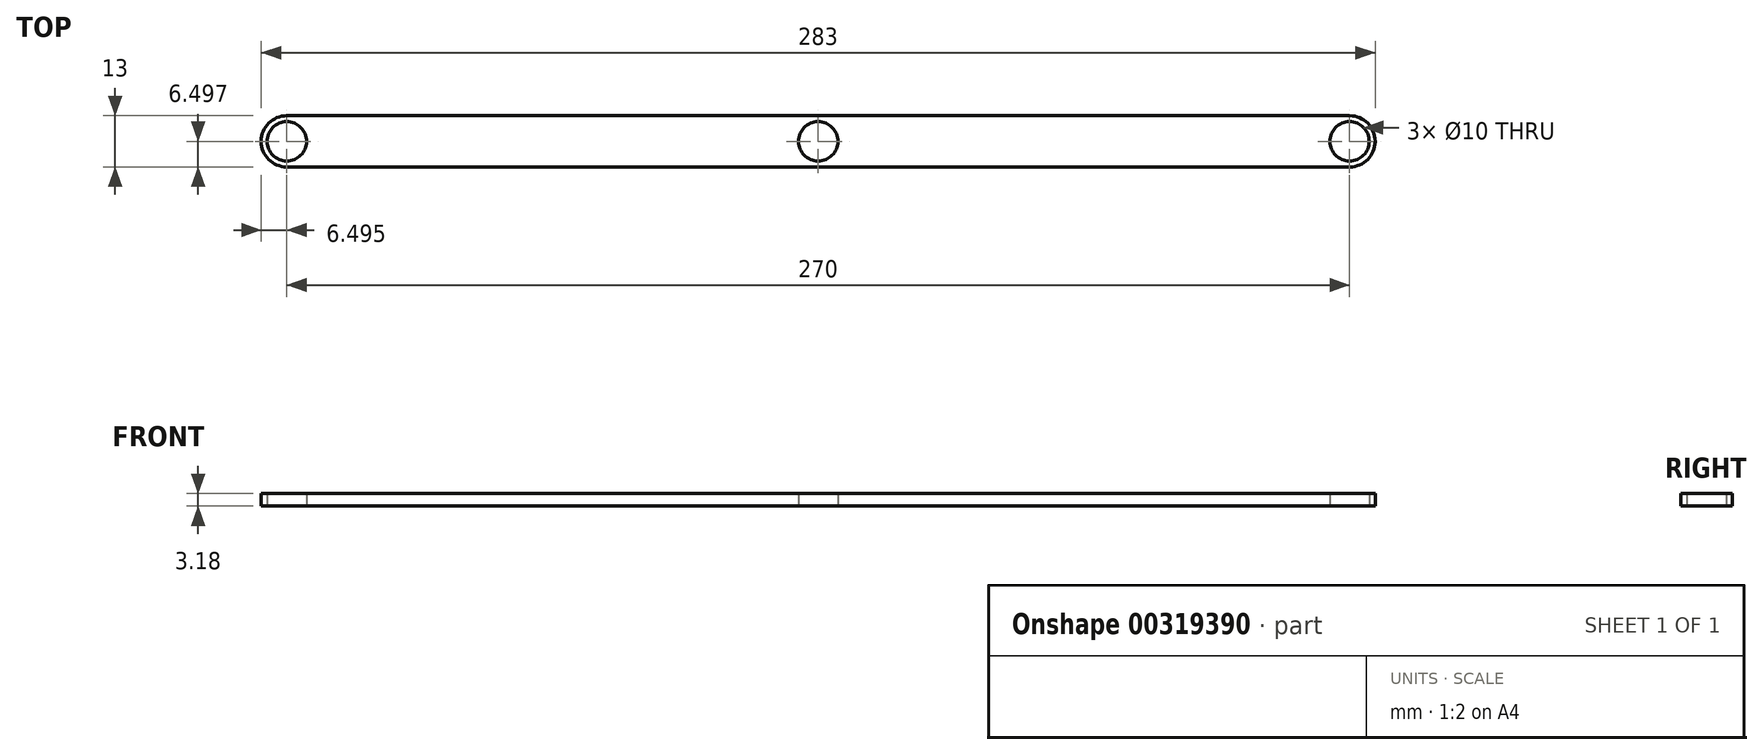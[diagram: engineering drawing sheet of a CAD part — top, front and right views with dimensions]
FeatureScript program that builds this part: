
annotation { "Feature Type Name" : "Feature", "Feature Type Description" : "" }
export const myFeature = defineFeature(function(context is Context, id is Id, definition is map)
    precondition{}
    {
        {
            var Q0;
            Q0=qCreatedBy(makeId("Top.planeOp"),FACE);
            var sketch = newSketch(context, id + "F0", { "sketchPlane" : qUnion([Q0])});
            skArc(sketch, "E0", {"start": v(-148.33, 25.07) * mm, "mid": v(-154.83, 18.57) * mm, "end": v(-148.33, 12.07) * mm});
            skCircle(sketch, "E1", {"center": v(-148.33, 18.57) * mm, "radius": 5 * mm});
            skLineSegment(sketch, "E2", {"start": v(-148.33, 25.07) * mm, "end": v(-80.83, 25.07) * mm});
            skLineSegment(sketch, "E3.MirrorCS", {"start": v(-148.33, 12.07) * mm, "end": v(-80.83, 12.07) * mm});
            skPoint(sketch, "E4.end.orphan", {"position": v(-80.83, 12.07) * mm});
            skPoint(sketch, "E4.start.orphan", {"position": v(-80.83, 25.07) * mm});
            skLineSegment(sketch, "E5.MirrorCS", {"start": v(-13.33, 12.07) * mm, "end": v(-80.83, 12.07) * mm});
            skLineSegment(sketch, "E6.MirrorCS", {"start": v(-13.33, 25.07) * mm, "end": v(-80.83, 25.07) * mm});
            skCircle(sketch, "E7.MirrorC", {"center": v(-13.33, 18.57) * mm, "radius": 5 * mm});
            skLineSegment(sketch, "E8.MirrorCS", {"start": v(-13.33, 25.07) * mm, "end": v(54.17, 25.07) * mm});
            skLineSegment(sketch, "E9.MirrorCS", {"start": v(-13.33, 12.07) * mm, "end": v(54.17, 12.07) * mm});
            skLineSegment(sketch, "E10.MirrorCS", {"start": v(121.67, 12.07) * mm, "end": v(54.17, 12.07) * mm});
            skLineSegment(sketch, "E11.MirrorCS", {"start": v(121.67, 25.07) * mm, "end": v(54.17, 25.07) * mm});
            skArc(sketch, "E12.MirrorCS", {"start": v(121.67, 25.07) * mm, "mid": v(128.17, 18.57) * mm, "end": v(121.67, 12.07) * mm});
            skCircle(sketch, "E13.MirrorC", {"center": v(121.67, 18.57) * mm, "radius": 5 * mm});
            skPoint(sketch, "E14.orphan", {"position": v(-13.33, 25.07) * mm});
            skPoint(sketch, "E15.MirrorCS.end.orphan", {"position": v(-13.33, 12.07) * mm});
            skSolve(sketch);
        }
        {
            var Q0;
            {var subQ1=sQuery(id+"F0.wireOp",EDGE,"E2");Q0=makeQuery(id+"F0.imprint","IMPRINT",FACE,{"disambiguationData":[TD([[makeQuery(id+"F0.imprint","IMPRINT",EDGE,{"derivedFrom":subQ1}),-1.0]])]});}
            var Q1;
            {var subQ0=sQuery(id+"F0.wireOp",EDGE,"E0");Q1=makeQuery(id+"F0.imprint","IMPRINT",FACE,{"disambiguationData":[TD([[makeQuery(id+"F0.imprint","IMPRINT",EDGE,{"derivedFrom":subQ0}),1.0]])]});}
            extrude(context, id + "F1", {"entities" : qUnion([Q0, Q1]), "depth" : 3.17 * mm});
        }
    });
